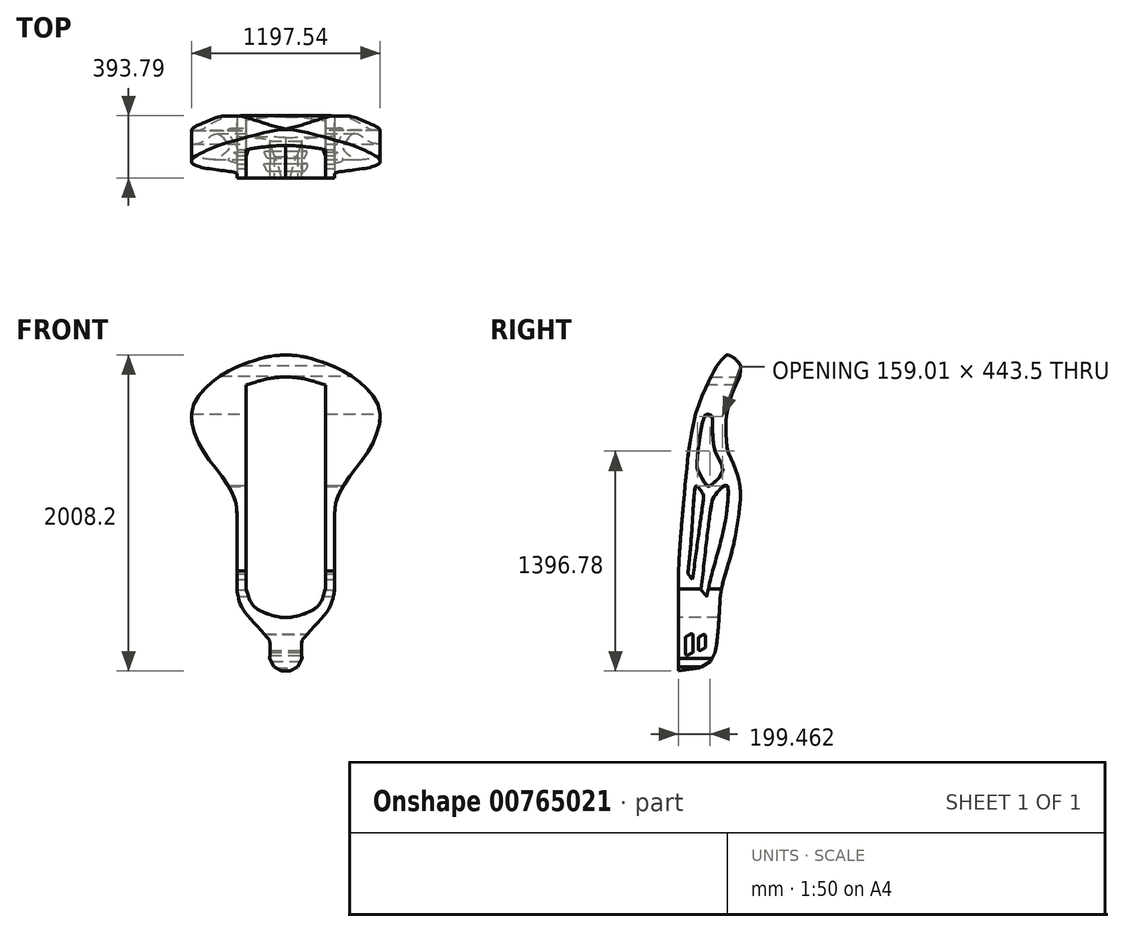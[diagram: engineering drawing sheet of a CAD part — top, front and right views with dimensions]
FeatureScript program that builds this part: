
annotation { "Feature Type Name" : "Feature", "Feature Type Description" : "" }
export const myFeature = defineFeature(function(context is Context, id is Id, definition is map)
    precondition{}
    {
        {
            var Q0;
            Q0=qCreatedBy(makeId("Front.planeOp"),FACE);
            var sketch = newSketch(context, id + "F0", { "sketchPlane" : qUnion([Q0])});
            skLineSegment(sketch, "E0", {"start": v(-255.28, -84.36) * mm, "end": v(252.72, -84.36) * mm});
            skLineSegment(sketch, "E1", {"start": v(0, -829.48) * mm, "end": v(0, 1173.27) * mm});
            skSolve(sketch);
        }
        {
            var Q0;
            Q0=qCreatedBy(makeId("Right.planeOp"),FACE);
            var sketch = newSketch(context, id + "F1", { "sketchPlane" : qUnion([Q0])});
            skLineSegment(sketch, "E2.0", {"start": v(0, -829.48) * mm, "end": v(0, 1173.27) * mm});
            skSolve(sketch);
        }
        {
            var Q0;
            Q0=qCreatedBy(makeId("Front.planeOp"),FACE);
            var sketch = newSketch(context, id + "F2", { "sketchPlane" : qUnion([Q0])});
            skFitSpline(sketch, "E3", {"points": [v(0, 1178.72) * mm, v(-131.61, 1163.15) * mm, v(-387.55, 1062.86) * mm, v(-534.54, 943.54) * mm, v(-586.42, 860.53) * mm, v(-598.52, 786.17) * mm, v(-593.33, 730.83) * mm, v(-536.94, 587.44) * mm, v(-445.29, 459.48) * mm, v(-334.61, 291.74) * mm, v(-310.9, 168.96) * mm], "startDerivative": vector(-1185.5, -55.3) * mm, "endDerivative": vector(0, -1218.83) * mm});
            skLineSegment(sketch, "E4", {"start": v(-310.9, 168.96) * mm, "end": v(-310.9, -308.33) * mm});
            skFitSpline(sketch, "E5", {"points": [v(-310.9, -308.33) * mm, v(-292.5, -393.37) * mm, v(-233.06, -486.5) * mm, v(-109.25, -625.95) * mm, v(-101.61, -641.2) * mm, v(-101.61, -747.96) * mm], "startDerivative": vector(68.26, -452.87) * mm, "endDerivative": vector(-14.07, -627.34) * mm});
            skLineSegment(sketch, "E6", {"start": v(-101.61, -747.96) * mm, "end": v(-75.98, -803.52) * mm});
            skLineSegment(sketch, "E7", {"start": v(-75.98, -803.52) * mm, "end": v(-19.8, -832.39) * mm});
            skLineSegment(sketch, "E8", {"start": v(-19.8, -832.39) * mm, "end": v(0, -832.39) * mm});
            skLineSegment(sketch, "E9", {"start": v(0, 1178.72) * mm, "end": v(0, -832.39) * mm, "construction": true});
            skLineSegment(sketch, "E10.MirrorCS", {"start": v(75.98, -803.52) * mm, "end": v(19.8, -832.39) * mm});
            skLineSegment(sketch, "E11.MirrorCS", {"start": v(101.61, -747.96) * mm, "end": v(75.98, -803.52) * mm});
            skLineSegment(sketch, "E12.MirrorCS", {"start": v(19.8, -832.39) * mm, "end": v(0, -832.39) * mm});
            skFitSpline(sketch, "E13.MirrorCS", {"points": [v(310.9, -308.33) * mm, v(292.5, -393.37) * mm, v(233.06, -486.5) * mm, v(109.25, -625.95) * mm, v(101.61, -641.2) * mm, v(101.61, -747.96) * mm], "startDerivative": vector(-68.26, -452.87) * mm, "endDerivative": vector(14.07, -627.34) * mm});
            skLineSegment(sketch, "E14.MirrorCS", {"start": v(310.9, 168.96) * mm, "end": v(310.9, -308.33) * mm});
            skFitSpline(sketch, "E15.MirrorCS", {"points": [v(0, 1178.72) * mm, v(131.61, 1163.15) * mm, v(387.55, 1062.86) * mm, v(534.54, 943.54) * mm, v(586.42, 860.53) * mm, v(598.52, 786.17) * mm, v(593.33, 730.83) * mm, v(536.94, 587.44) * mm, v(445.29, 459.48) * mm, v(334.61, 291.74) * mm, v(310.9, 168.96) * mm], "startDerivative": vector(1185.5, -55.3) * mm, "endDerivative": vector(0, -1218.83) * mm});
            skSolve(sketch);
        }
        {
            var Q0;
            Q0=qSketchRegion(id+"F2",true);
            extrude(context, id + "F3", {"entities" : qUnion([Q0]), "oppositeDirection" : true, "depth" : 523.24 * mm});
        }
        {
            var Q0;
            Q0=qCreatedBy(makeId("Right.planeOp"),FACE);
            var sketch = newSketch(context, id + "F4", { "sketchPlane" : qUnion([Q0])});
            skLineSegment(sketch, "E16.0", {"start": v(523.24, 1178.72) * mm, "end": v(0, 1178.72) * mm, "construction": true});
            skLineSegment(sketch, "E17.0", {"start": v(0, -829.48) * mm, "end": v(0, 1173.27) * mm, "construction": true});
            skFitSpline(sketch, "E18", {"points": [v(0, -829.48) * mm, v(0, -194.12) * mm, v(23.27, 143.63) * mm, v(62.09, 547.37) * mm, v(96.06, 753.12) * mm, v(140.7, 898.7) * mm, v(255.63, 1125.36) * mm, v(307.85, 1178.72) * mm], "startDerivative": vector(-39.4, 3171.5) * mm, "endDerivative": vector(647.49, 513.12) * mm});
            skFitSpline(sketch, "E19", {"points": [v(231.85, -711.1) * mm, v(246.25, -618.56) * mm, v(260.64, -421.14) * mm, v(272.98, -301.86) * mm, v(336.73, -75.65) * mm, v(375.8, 123.83) * mm, v(392.26, 269.84) * mm, v(390.2, 337.7) * mm, v(373.75, 417.9) * mm, v(338.79, 506.34) * mm, v(307.85, 586.06) * mm, v(301.76, 738.3) * mm, v(305.26, 807.25) * mm, v(341.33, 935.08) * mm, v(361.45, 984.12) * mm, v(390.27, 1044.51) * mm], "startDerivative": vector(248.18, 1330.22) * mm, "endDerivative": vector(610.21, 1265.5) * mm});
            skFitSpline(sketch, "E20", {"points": [v(307.85, 1178.72) * mm, v(350.06, 1159.99) * mm, v(393.79, 1113) * mm], "startDerivative": vector(77.42, 1.05) * mm, "endDerivative": vector(93.18, -122.51) * mm});
            skLineSegment(sketch, "E21", {"start": v(393.79, 1113) * mm, "end": v(390.27, 1044.51) * mm});
            skLineSegment(sketch, "E22", {"start": v(231.85, -711.1) * mm, "end": v(202.08, -767.87) * mm});
            skLineSegment(sketch, "E23", {"start": v(202.08, -767.87) * mm, "end": v(135.63, -809.16) * mm});
            skLineSegment(sketch, "E24", {"start": v(135.63, -809.16) * mm, "end": v(0, -829.48) * mm});
            skLineSegment(sketch, "E25.bottom", {"start": v(647.82, 1273) * mm, "end": v(-285.83, 1273) * mm});
            skLineSegment(sketch, "E25.top", {"start": v(647.82, -902.76) * mm, "end": v(-285.83, -902.76) * mm});
            skLineSegment(sketch, "E25.left", {"start": v(647.82, 1273) * mm, "end": v(647.82, -902.76) * mm});
            skLineSegment(sketch, "E25.right", {"start": v(-285.83, 1273) * mm, "end": v(-285.83, -902.76) * mm});
            skSolve(sketch);
        }
        {
            var Q0;
            Q0=qSketchRegion(id+"F4",true);
            extrude(context, id + "F5", {"entities" : qUnion([Q0]), "operationType" : NewBodyOperationType.REMOVE, "endBound" : BoundingType.THROUGH_ALL, "oppositeDirection" : true, "depth" : 25.4 * mm, "hasSecondDirection" : true, "secondDirectionBound" : SecondDirectionBoundingType.THROUGH_ALL, "secondDirectionOppositeDirection" : false, "secondDirectionDepth" : 25.4 * mm});
        }
        {
            var Q0;
            Q0=qCreatedBy(makeId("Front.planeOp"),FACE);
            var sketch = newSketch(context, id + "F6", { "sketchPlane" : qUnion([Q0])});
            skFitSpline(sketch, "E26.0.0", {"points": [v(310.9, 168.96) * mm, v(310.9, 172.92) * mm, v(311.01, 180.84) * mm, v(311.52, 192.71) * mm, v(312.42, 204.58) * mm, v(313.76, 216.32) * mm, v(315.53, 227.96) * mm, v(317.77, 239.47) * mm, v(320.48, 250.86) * mm, v(323.66, 262.14) * mm, v(327.32, 273.28) * mm, v(331.45, 284.3) * mm, v(334.9, 292.49) * mm, v(337.34, 297.9) * mm, v(339, 301.5) * mm, v(341.13, 305.97) * mm, v(343.77, 311.28) * mm, v(347.39, 318.29) * mm, v(353.96, 330.38) * mm, v(363.92, 347.25) * mm, v(376.6, 366.98) * mm, v(389.85, 386.32) * mm, v(403.55, 405.34) * mm, v(422.3, 430.35) * mm, v(441.63, 454.96) * mm, v(461.2, 479.4) * mm, v(475.83, 497.74) * mm, v(487.82, 513.17) * mm, v(497.17, 525.67) * mm, v(504.04, 535.15) * mm, v(509.62, 543.14) * mm, v(513.98, 549.6) * mm, v(517.2, 554.49) * mm, v(520.38, 559.4) * mm, v(524.51, 565.99) * mm, v(529.53, 574.29) * mm, v(535.3, 584.36) * mm, v(540.79, 594.54) * mm, v(546.04, 604.83) * mm, v(552.77, 618.66) * mm, v(560.68, 636.15) * mm, v(569.48, 657.43) * mm, v(576.26, 675.38) * mm, v(581.32, 689.88) * mm, v(584.93, 700.83) * mm, v(588.31, 711.88) * mm, v(591.41, 722.94) * mm, v(594.16, 734.03) * mm, v(596.4, 745.18) * mm, v(598, 756.4) * mm, v(598.64, 765.83) * mm, v(598.8, 773.4) * mm, v(598.75, 779.1) * mm, v(598.59, 784.81) * mm, v(598.34, 790.53) * mm, v(598.02, 796.22) * mm, v(597.48, 803.78) * mm, v(596.58, 813.15) * mm, v(595.1, 824.27) * mm, v(593.19, 835.25) * mm, v(590.76, 846.1) * mm, v(588.26, 855.02) * mm, v(585.92, 862.07) * mm, v(584.3, 866.44) * mm, v(582.93, 869.92) * mm, v(581.85, 872.52) * mm, v(580.74, 875.1) * mm, v(579.2, 878.5) * mm, v(577.19, 882.7) * mm, v(573.79, 889.32) * mm, v(569.22, 897.37) * mm, v(563.27, 906.73) * mm, v(556.93, 915.84) * mm, v(550.23, 924.73) * mm, v(544.4, 931.98) * mm, v(539.6, 937.7) * mm, v(535.95, 941.94) * mm, v(532.24, 946.15) * mm, v(527.24, 951.7) * mm, v(520.9, 958.53) * mm, v(510.5, 969.24) * mm, v(497.12, 982.22) * mm, v(483.2, 994.68) * mm, v(471.76, 1004.34) * mm, v(463.03, 1011.43) * mm, v(455.62, 1017.22) * mm, v(449.62, 1021.77) * mm, v(443.58, 1026.27) * mm, v(435.96, 1031.77) * mm, v(423.63, 1040.35) * mm, v(407.95, 1050.64) * mm, v(388.73, 1062.32) * mm, v(369.1, 1073.34) * mm, v(349.12, 1083.78) * mm, v(328.84, 1093.7) * mm, v(308.28, 1103.15) * mm, v(287.47, 1112.15) * mm, v(269.94, 1119.29) * mm, v(255.8, 1124.78) * mm, v(241.6, 1130.13) * mm, v(223.8, 1136.5) * mm, v(202.35, 1143.68) * mm, v(180.8, 1150.35) * mm, v(159.14, 1156.47) * mm, v(140.96, 1161.06) * mm, v(126.3, 1164.36) * mm, v(111.54, 1167.4) * mm, v(92.9, 1170.7) * mm, v(70.17, 1173.8) * mm, v(47.07, 1176.07) * mm, v(23.64, 1177.61) * mm, v(7.88, 1178.35) * mm, v(0, 1178.72) * mm]});
            skFitSpline(sketch, "E26.0.1", {"points": [v(0, 1178.72) * mm, v(-7.88, 1178.35) * mm, v(-23.64, 1177.61) * mm, v(-47.07, 1176.07) * mm, v(-70.17, 1173.8) * mm, v(-92.9, 1170.7) * mm, v(-111.54, 1167.4) * mm, v(-126.3, 1164.36) * mm, v(-140.96, 1161.06) * mm, v(-159.14, 1156.47) * mm, v(-180.8, 1150.35) * mm, v(-202.35, 1143.68) * mm, v(-223.8, 1136.5) * mm, v(-241.6, 1130.13) * mm, v(-255.8, 1124.78) * mm, v(-269.94, 1119.29) * mm, v(-287.47, 1112.15) * mm, v(-308.28, 1103.15) * mm, v(-328.84, 1093.7) * mm, v(-349.12, 1083.78) * mm, v(-369.1, 1073.34) * mm, v(-388.73, 1062.32) * mm, v(-407.95, 1050.64) * mm, v(-423.63, 1040.35) * mm, v(-435.96, 1031.77) * mm, v(-443.58, 1026.27) * mm, v(-449.62, 1021.77) * mm, v(-455.62, 1017.22) * mm, v(-463.03, 1011.43) * mm, v(-471.76, 1004.34) * mm, v(-483.2, 994.68) * mm, v(-497.12, 982.22) * mm, v(-510.5, 969.24) * mm, v(-520.9, 958.53) * mm, v(-527.24, 951.7) * mm, v(-532.24, 946.15) * mm, v(-535.95, 941.94) * mm, v(-539.6, 937.7) * mm, v(-544.4, 931.98) * mm, v(-550.23, 924.73) * mm, v(-556.93, 915.84) * mm, v(-563.27, 906.73) * mm, v(-569.22, 897.37) * mm, v(-573.79, 889.32) * mm, v(-577.19, 882.7) * mm, v(-579.2, 878.5) * mm, v(-580.74, 875.1) * mm, v(-581.85, 872.52) * mm, v(-582.93, 869.92) * mm, v(-584.3, 866.44) * mm, v(-585.92, 862.07) * mm, v(-588.26, 855.02) * mm, v(-590.76, 846.1) * mm, v(-593.19, 835.25) * mm, v(-595.1, 824.27) * mm, v(-596.58, 813.15) * mm, v(-597.48, 803.78) * mm, v(-598.02, 796.22) * mm, v(-598.34, 790.53) * mm, v(-598.59, 784.81) * mm, v(-598.75, 779.1) * mm, v(-598.8, 773.4) * mm, v(-598.64, 765.83) * mm, v(-598, 756.4) * mm, v(-596.4, 745.18) * mm, v(-594.16, 734.03) * mm, v(-591.41, 722.94) * mm, v(-588.31, 711.88) * mm, v(-584.93, 700.83) * mm, v(-581.32, 689.88) * mm, v(-576.26, 675.38) * mm, v(-569.48, 657.43) * mm, v(-560.68, 636.15) * mm, v(-552.77, 618.66) * mm, v(-546.04, 604.83) * mm, v(-540.79, 594.54) * mm, v(-535.3, 584.36) * mm, v(-529.53, 574.29) * mm, v(-524.51, 565.99) * mm, v(-520.38, 559.4) * mm, v(-517.2, 554.49) * mm, v(-513.98, 549.6) * mm, v(-509.62, 543.14) * mm, v(-504.04, 535.15) * mm, v(-497.17, 525.67) * mm, v(-487.82, 513.17) * mm, v(-475.83, 497.74) * mm, v(-461.2, 479.4) * mm, v(-441.63, 454.96) * mm, v(-422.3, 430.35) * mm, v(-403.55, 405.34) * mm, v(-389.85, 386.32) * mm, v(-376.6, 366.98) * mm, v(-363.92, 347.25) * mm, v(-353.96, 330.38) * mm, v(-347.39, 318.29) * mm, v(-343.77, 311.28) * mm, v(-341.13, 305.97) * mm, v(-339, 301.5) * mm, v(-337.34, 297.9) * mm, v(-334.9, 292.49) * mm, v(-331.45, 284.3) * mm, v(-327.32, 273.28) * mm, v(-323.66, 262.14) * mm, v(-320.48, 250.86) * mm, v(-317.77, 239.47) * mm, v(-315.53, 227.96) * mm, v(-313.76, 216.32) * mm, v(-312.42, 204.58) * mm, v(-311.52, 192.71) * mm, v(-311.01, 180.84) * mm, v(-310.9, 172.92) * mm, v(-310.9, 168.96) * mm]});
            skFitSpline(sketch, "E26.0.2", {"points": [v(-310.9, 1178.72) * mm, v(-310.9, 1165.88) * mm, v(-310.9, 1129.35) * mm, v(-310.9, 894.02) * mm, v(-310.9, 753.1) * mm, v(-310.9, 541.34) * mm, v(-310.9, 129.24) * mm, v(-310.9, -197.5) * mm, v(-310.9, -597.98) * mm, v(-310.9, -829.48) * mm]});
            skFitSpline(sketch, "E26.0.4", {"points": [v(310.9, 1178.72) * mm, v(310.9, 1165.88) * mm, v(310.9, 1129.35) * mm, v(310.9, 894.02) * mm, v(310.9, 753.1) * mm, v(310.9, 541.34) * mm, v(310.9, 129.24) * mm, v(310.9, -197.5) * mm, v(310.9, -597.98) * mm, v(310.9, -829.48) * mm]});
            skLineSegment(sketch, "E26.1.0", {"start": v(-25.46, -829.48) * mm, "end": v(25.46, -829.48) * mm});
            skLineSegment(sketch, "E26.1.1", {"start": v(25.46, -829.48) * mm, "end": v(75.98, -803.52) * mm});
            skLineSegment(sketch, "E26.1.2", {"start": v(75.98, -803.52) * mm, "end": v(101.61, -747.96) * mm});
            skFitSpline(sketch, "E26.1.3", {"points": [v(101.61, -747.96) * mm, v(100.6, -702.9) * mm, v(99.19, -639.84) * mm, v(107.99, -625.42) * mm, v(242.04, -482.32) * mm, v(297.07, -400.14) * mm, v(306.48, -337.69) * mm, v(310.9, -308.33) * mm]});
            skLineSegment(sketch, "E26.1.4", {"start": v(310.9, -308.33) * mm, "end": v(310.9, -194.12) * mm});
            skLineSegment(sketch, "E26.1.6", {"start": v(-310.9, -194.12) * mm, "end": v(-310.9, -308.33) * mm});
            skFitSpline(sketch, "E26.1.7", {"points": [v(-310.9, -308.33) * mm, v(-306.48, -337.69) * mm, v(-297.07, -400.14) * mm, v(-242.04, -482.32) * mm, v(-107.99, -625.42) * mm, v(-99.19, -639.84) * mm, v(-100.6, -702.9) * mm, v(-101.61, -747.96) * mm]});
            skLineSegment(sketch, "E26.1.8", {"start": v(-101.61, -747.96) * mm, "end": v(-75.98, -803.52) * mm});
            skLineSegment(sketch, "E26.1.9", {"start": v(-75.98, -803.52) * mm, "end": v(-25.46, -829.48) * mm});
            skFitSpline(sketch, "E27.0", {"points": [v(252.49, 1178.72) * mm, v(252.49, 1176.05) * mm, v(252.49, 1170.7) * mm, v(252.49, 1161.88) * mm, v(252.49, 1153.2) * mm, v(252.49, 1145.03) * mm, v(252.49, 1138.21) * mm, v(252.49, 1131.86) * mm, v(252.49, 1126.33) * mm, v(252.49, 1120.47) * mm, v(252.49, 1112.57) * mm, v(252.49, 1102.24) * mm, v(252.49, 1091.15) * mm, v(252.49, 1075.45) * mm, v(252.49, 1054.35) * mm, v(252.49, 1027.31) * mm, v(252.49, 999.24) * mm, v(252.49, 970.82) * mm, v(252.49, 947.39) * mm, v(252.49, 929.14) * mm, v(252.49, 915.78) * mm, v(252.49, 905) * mm, v(252.49, 896.62) * mm, v(252.49, 888.42) * mm, v(252.49, 878.47) * mm, v(252.49, 866.97) * mm, v(252.49, 855.86) * mm, v(252.49, 841.48) * mm, v(252.49, 824.18) * mm, v(252.49, 804.08) * mm, v(252.49, 787.52) * mm, v(252.49, 774.16) * mm, v(252.49, 764.04) * mm, v(252.49, 753.75) * mm, v(252.49, 743.24) * mm, v(252.49, 732.5) * mm, v(252.49, 717.85) * mm, v(252.49, 698.88) * mm, v(252.49, 674.93) * mm, v(252.49, 649.7) * mm, v(252.49, 623.06) * mm, v(252.49, 599.58) * mm, v(252.49, 579.97) * mm, v(252.49, 564.84) * mm, v(252.49, 549.27) * mm, v(252.49, 533.23) * mm, v(252.49, 516.77) * mm, v(252.49, 494.3) * mm, v(252.49, 465.33) * mm, v(252.49, 429.42) * mm, v(252.49, 392.65) * mm, v(252.49, 355.3) * mm, v(252.49, 317.67) * mm, v(252.49, 280.02) * mm, v(252.49, 242.64) * mm, v(252.49, 211.96) * mm, v(252.49, 187.83) * mm, v(252.49, 169.99) * mm, v(252.49, 152.41) * mm, v(252.49, 135.17) * mm, v(252.49, 118.24) * mm, v(252.49, 96.04) * mm, v(252.49, 68.88) * mm, v(252.49, 36.94) * mm, v(252.49, -5.2) * mm, v(252.49, -57.8) * mm, v(252.49, -123.23) * mm, v(252.49, -193.46) * mm, v(252.49, -270.92) * mm, v(252.49, -354.56) * mm, v(252.49, -443.36) * mm, v(252.49, -536.28) * mm, v(252.49, -632.3) * mm, v(252.49, -730.37) * mm, v(252.49, -796.44) * mm, v(252.49, -829.48) * mm]});
            skLineSegment(sketch, "E27.1", {"start": v(252.49, -303.95) * mm, "end": v(252.49, -194.12) * mm});
            skFitSpline(sketch, "E27.2", {"points": [v(-253.14, -299.62) * mm, v(-252.43, -304.34) * mm, v(-251.04, -313.59) * mm, v(-248.9, -326.83) * mm, v(-246.64, -339.34) * mm, v(-244.16, -351.04) * mm, v(-241.87, -360.01) * mm, v(-239.89, -366.7) * mm, v(-238.33, -371.44) * mm, v(-236.7, -375.92) * mm, v(-234.93, -380.29) * mm, v(-233, -384.62) * mm, v(-230.88, -388.98) * mm, v(-228.53, -393.45) * mm, v(-225.03, -399.6) * mm, v(-219.88, -407.83) * mm, v(-213.46, -417.01) * mm, v(-207.47, -425.05) * mm, v(-202.53, -431.45) * mm, v(-197.12, -438.24) * mm, v(-192.22, -444.24) * mm, v(-188.05, -449.27) * mm, v(-183.72, -454.44) * mm, v(-178.01, -461.17) * mm, v(-170.8, -469.55) * mm, v(-160.77, -481.06) * mm, v(-147.7, -495.86) * mm, v(-131.75, -513.7) * mm, v(-118.69, -528.15) * mm, v(-108.67, -539.2) * mm, v(-101.43, -547.18) * mm, v(-94.55, -554.77) * mm, v(-88.07, -561.91) * mm, v(-82.07, -568.55) * mm, v(-77.52, -573.61) * mm, v(-74.16, -577.37) * mm, v(-71.79, -580.04) * mm, v(-69.57, -582.55) * mm, v(-67.84, -584.52) * mm, v(-66.52, -586.03) * mm, v(-65.73, -586.95) * mm, v(-65.11, -587.67) * mm, v(-64.5, -588.38) * mm, v(-63.73, -589.3) * mm, v(-62.77, -590.45) * mm, v(-61.41, -592.1) * mm, v(-59.56, -594.43) * mm, v(-57.04, -597.86) * mm, v(-54.26, -602.1) * mm, v(-51.42, -607.18) * mm, v(-48.83, -612.85) * mm, v(-47.11, -617.68) * mm, v(-46.04, -621.36) * mm, v(-45.38, -623.98) * mm, v(-44.84, -626.43) * mm, v(-44.42, -628.7) * mm, v(-44.08, -630.78) * mm, v(-43.85, -632.37) * mm, v(-43.7, -633.57) * mm, v(-43.59, -634.43) * mm, v(-43.49, -635.27) * mm, v(-43.37, -636.39) * mm, v(-43.23, -637.76) * mm, v(-43.04, -639.93) * mm, v(-42.83, -642.61) * mm, v(-42.64, -645.86) * mm, v(-42.47, -649.16) * mm, v(-42.3, -653.68) * mm, v(-42.15, -659.57) * mm, v(-42.05, -667.07) * mm, v(-42.02, -675) * mm, v(-42.04, -683.35) * mm, v(-42.12, -692.08) * mm, v(-42.24, -701.12) * mm, v(-42.44, -713.55) * mm, v(-42.77, -729.62) * mm, v(-43.06, -742.74) * mm, v(-43.2, -749.27) * mm]});
            skLineSegment(sketch, "E27.3", {"start": v(-252.49, -194.12) * mm, "end": v(-252.49, -303.95) * mm});
            skFitSpline(sketch, "E27.4", {"points": [v(-252.49, 1178.72) * mm, v(-252.49, 1176.05) * mm, v(-252.49, 1170.7) * mm, v(-252.49, 1161.88) * mm, v(-252.49, 1153.2) * mm, v(-252.49, 1145.03) * mm, v(-252.49, 1138.21) * mm, v(-252.49, 1131.86) * mm, v(-252.49, 1126.33) * mm, v(-252.49, 1120.47) * mm, v(-252.49, 1112.57) * mm, v(-252.49, 1102.24) * mm, v(-252.49, 1091.15) * mm, v(-252.49, 1075.45) * mm, v(-252.49, 1054.35) * mm, v(-252.49, 1027.31) * mm, v(-252.49, 999.24) * mm, v(-252.49, 970.82) * mm, v(-252.49, 947.39) * mm, v(-252.49, 929.14) * mm, v(-252.49, 915.78) * mm, v(-252.49, 905) * mm, v(-252.49, 896.62) * mm, v(-252.49, 888.42) * mm, v(-252.49, 878.47) * mm, v(-252.49, 866.97) * mm, v(-252.49, 855.86) * mm, v(-252.49, 841.48) * mm, v(-252.49, 824.18) * mm, v(-252.49, 804.08) * mm, v(-252.49, 787.52) * mm, v(-252.49, 774.16) * mm, v(-252.49, 764.04) * mm, v(-252.49, 753.75) * mm, v(-252.49, 743.24) * mm, v(-252.49, 732.5) * mm, v(-252.49, 717.85) * mm, v(-252.49, 698.88) * mm, v(-252.49, 674.93) * mm, v(-252.49, 649.7) * mm, v(-252.49, 623.06) * mm, v(-252.49, 599.58) * mm, v(-252.49, 579.97) * mm, v(-252.49, 564.84) * mm, v(-252.49, 549.27) * mm, v(-252.49, 533.23) * mm, v(-252.49, 516.77) * mm, v(-252.49, 494.3) * mm, v(-252.49, 465.33) * mm, v(-252.49, 429.42) * mm, v(-252.49, 392.65) * mm, v(-252.49, 355.3) * mm, v(-252.49, 317.67) * mm, v(-252.49, 280.02) * mm, v(-252.49, 242.64) * mm, v(-252.49, 211.96) * mm, v(-252.49, 187.83) * mm, v(-252.49, 169.99) * mm, v(-252.49, 152.41) * mm, v(-252.49, 135.17) * mm, v(-252.49, 118.24) * mm, v(-252.49, 96.04) * mm, v(-252.49, 68.88) * mm, v(-252.49, 36.94) * mm, v(-252.49, -5.2) * mm, v(-252.49, -57.8) * mm, v(-252.49, -123.23) * mm, v(-252.49, -193.46) * mm, v(-252.49, -270.92) * mm, v(-252.49, -354.56) * mm, v(-252.49, -443.36) * mm, v(-252.49, -536.28) * mm, v(-252.49, -632.3) * mm, v(-252.49, -730.37) * mm, v(-252.49, -796.44) * mm, v(-252.49, -829.48) * mm]});
            skFitSpline(sketch, "E27.5", {"points": [v(2.72, 1120.36) * mm, v(-1.21, 1120.18) * mm, v(-7.05, 1119.9) * mm, v(-14.68, 1119.52) * mm, v(-20.33, 1119.22) * mm, v(-25.9, 1118.89) * mm, v(-31.42, 1118.53) * mm, v(-36.87, 1118.15) * mm, v(-42.26, 1117.73) * mm, v(-47.59, 1117.27) * mm, v(-52.88, 1116.77) * mm, v(-58.13, 1116.23) * mm, v(-63.33, 1115.65) * mm, v(-68.49, 1115.02) * mm, v(-73.62, 1114.34) * mm, v(-78.73, 1113.62) * mm, v(-83.81, 1112.85) * mm, v(-88.87, 1112.03) * mm, v(-95.6, 1110.88) * mm, v(-102.29, 1109.63) * mm, v(-108.96, 1108.29) * mm, v(-113.95, 1107.23) * mm, v(-118.94, 1106.13) * mm, v(-125.6, 1104.6) * mm, v(-132.29, 1102.97) * mm, v(-138.98, 1101.26) * mm, v(-144.02, 1099.93) * mm, v(-149.06, 1098.57) * mm, v(-155.79, 1096.7) * mm, v(-167.57, 1093.29) * mm, v(-184.44, 1088.07) * mm, v(-201.3, 1082.43) * mm, v(-214.77, 1077.69) * mm, v(-224.86, 1074) * mm, v(-234.94, 1070.21) * mm, v(-244.96, 1066.32) * mm, v(-254.93, 1062.32) * mm, v(-268.14, 1056.86) * mm, v(-284.5, 1049.79) * mm, v(-303.81, 1040.91) * mm, v(-319.6, 1033.18) * mm, v(-332.03, 1026.8) * mm, v(-341.23, 1021.9) * mm, v(-348.78, 1017.73) * mm, v(-354.76, 1014.34) * mm, v(-359.2, 1011.77) * mm, v(-363.6, 1009.17) * mm, v(-369.46, 1005.65) * mm, v(-376.7, 1001.16) * mm, v(-385.3, 995.63) * mm, v(-393.78, 989.95) * mm, v(-402.17, 984.12) * mm, v(-409.06, 979.13) * mm, v(-414.52, 975.07) * mm, v(-419.95, 970.95) * mm, v(-426.63, 965.73) * mm, v(-434.5, 959.34) * mm, v(-444.8, 950.64) * mm, v(-457.3, 939.46) * mm, v(-469.27, 927.85) * mm, v(-477.37, 919.5) * mm, v(-481.91, 914.66) * mm, v(-485.28, 911) * mm, v(-488.6, 907.3) * mm, v(-491.89, 903.58) * mm, v(-495.09, 899.85) * mm, v(-498.2, 896.15) * mm, v(-501.2, 892.47) * mm, v(-505.08, 887.57) * mm, v(-509.64, 881.51) * mm, v(-514.65, 874.32) * mm, v(-519.15, 867.22) * mm, v(-522.46, 861.37) * mm, v(-524.86, 856.71) * mm, v(-526.25, 853.8) * mm, v(-527.3, 851.48) * mm, v(-528.06, 849.73) * mm, v(-528.78, 847.98) * mm, v(-529.47, 846.24) * mm, v(-530.13, 844.5) * mm, v(-530.75, 842.77) * mm, v(-531.34, 841.03) * mm, v(-532.1, 838.66) * mm, v(-532.83, 836.23) * mm, v(-533.52, 833.72) * mm, v(-534.18, 831.17) * mm, v(-534.96, 827.9) * mm, v(-536.1, 822.48) * mm, v(-537.34, 815.44) * mm, v(-538.33, 808.04) * mm, v(-538.97, 801.94) * mm, v(-539.3, 798.05) * mm, v(-539.55, 794.89) * mm, v(-539.7, 792.5) * mm, v(-539.85, 790.09) * mm, v(-539.96, 788.05) * mm, v(-540.04, 786.42) * mm, v(-540.1, 785.19) * mm, v(-540.14, 783.96) * mm, v(-540.19, 782.73) * mm, v(-540.23, 781.52) * mm, v(-540.28, 779.94) * mm, v(-540.32, 778.03) * mm, v(-540.35, 775.84) * mm, v(-540.35, 773.74) * mm, v(-540.33, 772.07) * mm, v(-540.3, 770.77) * mm, v(-540.27, 769.82) * mm, v(-540.23, 768.9) * mm, v(-540.17, 767.65) * mm, v(-540.08, 766.12) * mm, v(-539.96, 764.6) * mm, v(-539.85, 763.4) * mm, v(-539.76, 762.51) * mm, v(-539.66, 761.62) * mm, v(-539.52, 760.4) * mm, v(-539.32, 758.88) * mm, v(-539.04, 757) * mm, v(-538.73, 755.07) * mm, v(-538.37, 753.1) * mm, v(-537.85, 750.4) * mm, v(-537.25, 747.59) * mm, v(-536.58, 744.67) * mm, v(-536.04, 742.44) * mm, v(-535.47, 740.17) * mm, v(-534.87, 737.85) * mm, v(-534.24, 735.5) * mm, v(-533.59, 733.13) * mm, v(-532.91, 730.74) * mm, v(-531.98, 727.52) * mm, v(-530.76, 723.46) * mm, v(-528.71, 716.9) * mm, v(-526, 708.66) * mm, v(-523.11, 700.39) * mm, v(-520.71, 693.78) * mm, v(-518.87, 688.83) * mm, v(-516.98, 683.89) * mm, v(-515.05, 678.96) * mm, v(-513.09, 674.04) * mm, v(-511.08, 669.14) * mm, v(-509.04, 664.27) * mm, v(-506.96, 659.4) * mm, v(-504.85, 654.58) * mm, v(-502.7, 649.77) * mm, v(-500.5, 645) * mm, v(-497.54, 638.68) * mm, v(-494.5, 632.43) * mm, v(-491.4, 626.28) * mm, v(-489.03, 621.71) * mm, v(-487.03, 617.96) * mm, v(-485.41, 614.97) * mm, v(-484.19, 612.75) * mm, v(-482.95, 610.54) * mm, v(-481.27, 607.6) * mm, v(-479.14, 603.92) * mm, v(-476.52, 599.52) * mm, v(-473.84, 595.15) * mm, v(-471.1, 590.78) * mm, v(-468.28, 586.41) * mm, v(-465.4, 582.06) * mm, v(-461.49, 576.26) * mm, v(-454.42, 566.13) * mm, v(-445.86, 554.52) * mm, v(-436.86, 542.8) * mm, v(-429.92, 533.92) * mm, v(-422.81, 524.96) * mm, v(-416.78, 517.4) * mm, v(-411.9, 511.3) * mm, v(-408.23, 506.71) * mm, v(-404.54, 502.09) * mm, v(-400.83, 497.44) * mm, v(-397.12, 492.76) * mm, v(-392.16, 486.5) * mm, v(-385.98, 478.63) * mm, v(-378.56, 469.1) * mm, v(-371.18, 459.47) * mm, v(-363.83, 449.75) * mm, v(-354.1, 436.64) * mm, v(-344.48, 423.3) * mm, v(-335.01, 409.65) * mm, v(-329.17, 400.98) * mm, v(-324.55, 393.95) * mm, v(-321.1, 388.63) * mm, v(-317.69, 383.25) * mm, v(-314.3, 377.82) * mm, v(-310.95, 372.33) * mm, v(-307.63, 366.76) * mm, v(-304.35, 361.12) * mm, v(-301.11, 355.4) * mm, v(-297.92, 349.6) * mm, v(-294.77, 343.7) * mm, v(-291.67, 337.7) * mm, v(-288.62, 331.58) * mm, v(-286.13, 326.37) * mm, v(-284.18, 322.14) * mm, v(-282.74, 318.93) * mm, v(-281.32, 315.7) * mm, v(-279.93, 312.45) * mm, v(-278.57, 309.18) * mm, v(-276.8, 304.8) * mm, v(-274.67, 299.29) * mm, v(-272.26, 292.63) * mm, v(-269.98, 285.93) * mm, v(-267.13, 276.92) * mm, v(-263.92, 265.57) * mm, v(-260.65, 251.8) * mm, v(-257.96, 237.93) * mm, v(-256.18, 226.33) * mm, v(-255.04, 217.04) * mm, v(-254.07, 207.74) * mm, v(-253.19, 196.15) * mm, v(-252.6, 182.43) * mm, v(-252.49, 173.42) * mm, v(-252.49, 168.96) * mm]});
            skLineSegment(sketch, "E27.6", {"start": v(-42.9, -735.75) * mm, "end": v(-31.37, -760.76) * mm});
            skLineSegment(sketch, "E27.7", {"start": v(-31.37, -760.76) * mm, "end": v(-11.33, -771.06) * mm});
            skFitSpline(sketch, "E27.8", {"points": [v(252.49, 168.96) * mm, v(252.49, 173.42) * mm, v(252.6, 182.43) * mm, v(253.19, 196.15) * mm, v(254.07, 207.74) * mm, v(255.04, 217.04) * mm, v(256.18, 226.33) * mm, v(257.96, 237.93) * mm, v(260.65, 251.8) * mm, v(263.92, 265.57) * mm, v(267.13, 276.92) * mm, v(269.98, 285.93) * mm, v(272.26, 292.63) * mm, v(274.67, 299.29) * mm, v(276.8, 304.8) * mm, v(278.57, 309.18) * mm, v(279.93, 312.45) * mm, v(281.32, 315.7) * mm, v(282.74, 318.93) * mm, v(284.18, 322.14) * mm, v(286.13, 326.37) * mm, v(288.62, 331.58) * mm, v(291.67, 337.7) * mm, v(294.77, 343.7) * mm, v(297.92, 349.6) * mm, v(301.11, 355.4) * mm, v(304.35, 361.12) * mm, v(307.63, 366.76) * mm, v(310.95, 372.33) * mm, v(314.3, 377.82) * mm, v(317.69, 383.25) * mm, v(321.1, 388.63) * mm, v(324.55, 393.95) * mm, v(329.17, 400.98) * mm, v(335.01, 409.65) * mm, v(344.48, 423.3) * mm, v(354.1, 436.64) * mm, v(363.83, 449.75) * mm, v(371.18, 459.47) * mm, v(378.56, 469.1) * mm, v(385.98, 478.63) * mm, v(392.16, 486.5) * mm, v(397.12, 492.76) * mm, v(400.83, 497.44) * mm, v(404.54, 502.09) * mm, v(408.23, 506.71) * mm, v(411.9, 511.3) * mm, v(416.78, 517.4) * mm, v(422.81, 524.96) * mm, v(429.92, 533.92) * mm, v(436.86, 542.8) * mm, v(445.86, 554.52) * mm, v(454.42, 566.13) * mm, v(461.49, 576.26) * mm, v(465.4, 582.06) * mm, v(468.28, 586.41) * mm, v(471.1, 590.78) * mm, v(473.84, 595.15) * mm, v(476.52, 599.52) * mm, v(479.14, 603.92) * mm, v(481.27, 607.6) * mm, v(482.95, 610.54) * mm, v(484.19, 612.75) * mm, v(485.41, 614.97) * mm, v(487.03, 617.96) * mm, v(489.03, 621.71) * mm, v(491.4, 626.28) * mm, v(494.5, 632.43) * mm, v(497.54, 638.68) * mm, v(500.5, 645) * mm, v(502.7, 649.77) * mm, v(504.85, 654.58) * mm, v(506.96, 659.4) * mm, v(509.04, 664.27) * mm, v(511.08, 669.14) * mm, v(513.09, 674.04) * mm, v(515.05, 678.96) * mm, v(516.98, 683.89) * mm, v(518.87, 688.83) * mm, v(520.71, 693.78) * mm, v(523.11, 700.39) * mm, v(526, 708.66) * mm, v(528.71, 716.9) * mm, v(530.76, 723.46) * mm, v(531.98, 727.52) * mm, v(532.91, 730.74) * mm, v(533.59, 733.13) * mm, v(534.24, 735.5) * mm, v(534.87, 737.85) * mm, v(535.47, 740.17) * mm, v(536.04, 742.44) * mm, v(536.58, 744.67) * mm, v(537.25, 747.59) * mm, v(537.85, 750.4) * mm, v(538.37, 753.1) * mm, v(538.73, 755.07) * mm, v(539.04, 757) * mm, v(539.32, 758.88) * mm, v(539.52, 760.4) * mm, v(539.66, 761.62) * mm, v(539.76, 762.51) * mm, v(539.85, 763.4) * mm, v(539.96, 764.6) * mm, v(540.08, 766.12) * mm, v(540.17, 767.65) * mm, v(540.23, 768.9) * mm, v(540.27, 769.82) * mm, v(540.3, 770.77) * mm, v(540.33, 772.07) * mm, v(540.35, 773.74) * mm, v(540.35, 775.84) * mm, v(540.32, 778.03) * mm, v(540.28, 779.94) * mm, v(540.23, 781.52) * mm, v(540.19, 782.73) * mm, v(540.14, 783.96) * mm, v(540.1, 785.19) * mm, v(540.04, 786.42) * mm, v(539.96, 788.05) * mm, v(539.85, 790.09) * mm, v(539.7, 792.5) * mm, v(539.55, 794.89) * mm, v(539.3, 798.05) * mm, v(538.97, 801.94) * mm, v(538.33, 808.04) * mm, v(537.34, 815.44) * mm, v(536.1, 822.48) * mm, v(534.96, 827.9) * mm, v(534.18, 831.17) * mm, v(533.52, 833.72) * mm, v(532.83, 836.23) * mm, v(532.1, 838.66) * mm, v(531.34, 841.03) * mm, v(530.75, 842.77) * mm, v(530.13, 844.5) * mm, v(529.47, 846.24) * mm, v(528.78, 847.98) * mm, v(528.06, 849.73) * mm, v(527.3, 851.48) * mm, v(526.25, 853.8) * mm, v(524.86, 856.71) * mm, v(522.46, 861.37) * mm, v(519.15, 867.22) * mm, v(514.65, 874.32) * mm, v(509.64, 881.51) * mm, v(505.08, 887.57) * mm, v(501.2, 892.47) * mm, v(498.2, 896.15) * mm, v(495.09, 899.85) * mm, v(491.89, 903.58) * mm, v(488.6, 907.3) * mm, v(485.28, 911) * mm, v(481.91, 914.66) * mm, v(477.37, 919.5) * mm, v(469.27, 927.85) * mm, v(457.3, 939.46) * mm, v(444.8, 950.64) * mm, v(434.5, 959.34) * mm, v(426.63, 965.73) * mm, v(419.95, 970.95) * mm, v(414.52, 975.07) * mm, v(409.06, 979.13) * mm, v(402.17, 984.12) * mm, v(393.78, 989.95) * mm, v(385.3, 995.63) * mm, v(376.7, 1001.16) * mm, v(369.46, 1005.65) * mm, v(363.6, 1009.17) * mm, v(359.2, 1011.77) * mm, v(354.76, 1014.34) * mm, v(348.78, 1017.73) * mm, v(341.23, 1021.9) * mm, v(332.03, 1026.8) * mm, v(319.6, 1033.18) * mm, v(303.81, 1040.91) * mm, v(284.5, 1049.79) * mm, v(268.14, 1056.86) * mm, v(254.93, 1062.32) * mm, v(244.96, 1066.32) * mm, v(234.94, 1070.21) * mm, v(224.86, 1074) * mm, v(214.77, 1077.69) * mm, v(201.3, 1082.43) * mm, v(184.44, 1088.07) * mm, v(167.57, 1093.29) * mm, v(155.79, 1096.7) * mm, v(149.06, 1098.57) * mm, v(144.02, 1099.93) * mm, v(138.98, 1101.26) * mm, v(132.29, 1102.97) * mm, v(125.6, 1104.6) * mm, v(118.94, 1106.13) * mm, v(113.95, 1107.23) * mm, v(108.96, 1108.29) * mm, v(102.29, 1109.63) * mm, v(95.6, 1110.88) * mm, v(88.87, 1112.03) * mm, v(83.81, 1112.85) * mm, v(78.73, 1113.62) * mm, v(73.62, 1114.34) * mm, v(68.49, 1115.02) * mm, v(63.33, 1115.65) * mm, v(58.13, 1116.23) * mm, v(52.88, 1116.77) * mm, v(47.59, 1117.27) * mm, v(42.26, 1117.73) * mm, v(36.87, 1118.15) * mm, v(31.42, 1118.53) * mm, v(25.9, 1118.89) * mm, v(20.33, 1119.22) * mm, v(14.68, 1119.52) * mm, v(7.05, 1119.9) * mm, v(1.21, 1120.18) * mm, v(-2.72, 1120.36) * mm]});
            skLineSegment(sketch, "E27.9", {"start": v(-11.33, -771.06) * mm, "end": v(11.33, -771.06) * mm});
            skLineSegment(sketch, "E27.10", {"start": v(11.33, -771.06) * mm, "end": v(31.37, -760.76) * mm});
            skLineSegment(sketch, "E27.11", {"start": v(31.37, -760.76) * mm, "end": v(42.9, -735.75) * mm});
            skFitSpline(sketch, "E27.12", {"points": [v(43.2, -749.27) * mm, v(43.06, -742.74) * mm, v(42.77, -729.62) * mm, v(42.44, -713.55) * mm, v(42.24, -701.12) * mm, v(42.12, -692.08) * mm, v(42.04, -683.35) * mm, v(42.02, -675) * mm, v(42.05, -667.07) * mm, v(42.15, -659.57) * mm, v(42.3, -653.68) * mm, v(42.47, -649.16) * mm, v(42.64, -645.86) * mm, v(42.83, -642.61) * mm, v(43.04, -639.93) * mm, v(43.23, -637.76) * mm, v(43.37, -636.39) * mm, v(43.49, -635.27) * mm, v(43.59, -634.43) * mm, v(43.7, -633.57) * mm, v(43.85, -632.37) * mm, v(44.08, -630.78) * mm, v(44.42, -628.7) * mm, v(44.84, -626.43) * mm, v(45.38, -623.98) * mm, v(46.04, -621.36) * mm, v(47.11, -617.68) * mm, v(48.83, -612.85) * mm, v(51.42, -607.18) * mm, v(54.26, -602.1) * mm, v(57.04, -597.86) * mm, v(59.56, -594.43) * mm, v(61.41, -592.1) * mm, v(62.77, -590.45) * mm, v(63.73, -589.3) * mm, v(64.5, -588.38) * mm, v(65.11, -587.67) * mm, v(65.73, -586.95) * mm, v(66.52, -586.03) * mm, v(67.84, -584.52) * mm, v(69.57, -582.55) * mm, v(71.79, -580.04) * mm, v(74.16, -577.37) * mm, v(77.52, -573.61) * mm, v(82.07, -568.55) * mm, v(88.07, -561.91) * mm, v(94.55, -554.77) * mm, v(101.43, -547.18) * mm, v(108.67, -539.2) * mm, v(118.69, -528.15) * mm, v(131.75, -513.7) * mm, v(147.7, -495.86) * mm, v(160.77, -481.06) * mm, v(170.8, -469.55) * mm, v(178.01, -461.17) * mm, v(183.72, -454.44) * mm, v(188.05, -449.27) * mm, v(192.22, -444.24) * mm, v(197.12, -438.24) * mm, v(202.53, -431.45) * mm, v(207.47, -425.05) * mm, v(213.46, -417.01) * mm, v(219.88, -407.83) * mm, v(225.03, -399.6) * mm, v(228.53, -393.45) * mm, v(230.88, -388.98) * mm, v(233, -384.62) * mm, v(234.93, -380.29) * mm, v(236.7, -375.92) * mm, v(238.33, -371.44) * mm, v(239.89, -366.7) * mm, v(241.87, -360.01) * mm, v(244.16, -351.04) * mm, v(246.64, -339.34) * mm, v(248.9, -326.83) * mm, v(251.04, -313.59) * mm, v(252.43, -304.34) * mm, v(253.14, -299.62) * mm]});
            skFitSpline(sketch, "E28", {"points": [v(-533.6, 733.18) * mm, v(-538.35, 807.6) * mm, v(-445.42, 899.69) * mm, v(-126.67, 1025.13) * mm, v(0, 1037.47) * mm], "startDerivative": vector(-100.12, 437.17) * mm, "endDerivative": vector(474.07, -1.36) * mm});
            skFitSpline(sketch, "E29", {"points": [v(-252.49, -303.95) * mm, v(-214.34, -403.54) * mm, v(-149.63, -452.26) * mm, v(-45.66, -485.7) * mm, v(0, -489.34) * mm], "startDerivative": vector(108.5, -392.67) * mm, "endDerivative": vector(217.04, -1.44) * mm});
            skLineSegment(sketch, "E30.0", {"start": v(0, -829.48) * mm, "end": v(0, 1173.27) * mm, "construction": true});
            skFitSpline(sketch, "E31.MirrorCS", {"points": [v(252.49, -303.95) * mm, v(214.34, -403.54) * mm, v(149.63, -452.26) * mm, v(45.66, -485.7) * mm, v(0, -489.34) * mm], "startDerivative": vector(-108.5, -392.67) * mm, "endDerivative": vector(-217.04, -1.44) * mm});
            skFitSpline(sketch, "E32.MirrorCS", {"points": [v(533.6, 733.18) * mm, v(538.35, 807.6) * mm, v(445.42, 899.69) * mm, v(126.67, 1025.13) * mm, v(0, 1037.47) * mm], "startDerivative": vector(100.12, 437.17) * mm, "endDerivative": vector(-474.07, -1.36) * mm});
            skSolve(sketch);
        }
        {
            var Q0;
            {var subQ14=sQuery(id+"F6.wireOp",EDGE,"E27.0");Q0=makeQuery(id+"F6.imprint","IMPRINT",FACE,{"disambiguationData":[TD([[makeQuery(id+"F6.imprint","IMPRINT",EDGE,{"derivedFrom":subQ14}),-1.0]])]});}
            extrude(context, id + "F7", {"entities" : qUnion([Q0]), "operationType" : NewBodyOperationType.REMOVE, "oppositeDirection" : true, "depth" : 617.22 * mm});
        }
        {
            var Q0;
            Q0=qCreatedBy(makeId("Right.planeOp"),FACE);
            var sketch = newSketch(context, id + "F8", { "sketchPlane" : qUnion([Q0])});
            skFitSpline(sketch, "E33", {"points": [v(278.97, 437.84) * mm, v(239.7, 546.9) * mm, v(216.44, 666.14) * mm, v(214.99, 762.12) * mm, v(212.08, 791.2) * mm, v(185.9, 802.83) * mm, v(162.64, 786.84) * mm, v(114.65, 475.65) * mm, v(121.92, 446.56) * mm, v(180.09, 346.23) * mm, v(201.9, 350.59) * mm, v(278.97, 437.84) * mm]});
            skFitSpline(sketch, "E34", {"points": [v(178.15, -355.19) * mm, v(211.05, -215.34) * mm, v(256.3, -48.77) * mm, v(298.84, 138.5) * mm, v(315.3, 306.1) * mm, v(308.1, 346.2) * mm, v(289.59, 348.26) * mm, v(227.9, 282.45) * mm, v(213.5, 254.69) * mm, v(142.55, -313.93) * mm], "startDerivative": vector(260.8, 1163.28) * mm, "endDerivative": vector(-357.18, -3242.65) * mm});
            skFitSpline(sketch, "E35", {"points": [v(178.15, -355.19) * mm, v(142.55, -313.93) * mm, v(88.15, -248.93) * mm, v(59.04, -211.08) * mm], "startDerivative": vector(-104.4, 120.4) * mm, "endDerivative": vector(-88.09, 117.81) * mm});
            skFitSpline(sketch, "E36", {"points": [v(88.15, -248.93) * mm, v(157.06, 256.72) * mm, v(156.1, 292.63) * mm, v(124.84, 337.91) * mm, v(112.58, 347.17) * mm, v(104.41, 330.29) * mm, v(84.68, 77.24) * mm, v(59.04, -211.08) * mm], "startDerivative": vector(302.64, 2248.83) * mm, "endDerivative": vector(-126.04, -1237.86) * mm});
            skLineSegment(sketch, "E37", {"start": v(170.59, -675.29) * mm, "end": v(170.59, -606.61) * mm});
            skLineSegment(sketch, "E38", {"start": v(156.62, -598.2) * mm, "end": v(130.78, -611.83) * mm});
            skLineSegment(sketch, "E39", {"start": v(125.7, -620.26) * mm, "end": v(125.7, -688.93) * mm});
            skLineSegment(sketch, "E40", {"start": v(139.68, -697.35) * mm, "end": v(165.51, -683.71) * mm});
            skLineSegment(sketch, "E41", {"start": v(91.74, -602.48) * mm, "end": v(91.74, -704.81) * mm});
            skLineSegment(sketch, "E42", {"start": v(86.66, -713.24) * mm, "end": v(57.67, -728.55) * mm});
            skLineSegment(sketch, "E43", {"start": v(43.7, -720.12) * mm, "end": v(43.7, -617.79) * mm});
            skLineSegment(sketch, "E44", {"start": v(48.77, -609.36) * mm, "end": v(77.77, -594.05) * mm});
            skPoint(sketch, "E45.visualSharp", {"position": v(170.59, -681.03) * mm});
            skArc(sketch, "E45.filletArc", {"start": v(165.51, -683.71) * mm, "mid": v(169.22, -680.2) * mm, "end": v(170.59, -675.29) * mm});
            skPoint(sketch, "E46.visualSharp", {"position": v(125.7, -614.51) * mm});
            skArc(sketch, "E46.filletArc", {"start": v(130.78, -611.83) * mm, "mid": v(127.07, -615.34) * mm, "end": v(125.7, -620.26) * mm});
            skPoint(sketch, "E47.visualSharp", {"position": v(125.7, -704.73) * mm});
            skArc(sketch, "E47.filletArc", {"start": v(125.7, -688.93) * mm, "mid": v(130.32, -697.09) * mm, "end": v(139.68, -697.35) * mm});
            skPoint(sketch, "E48.visualSharp", {"position": v(170.59, -590.81) * mm});
            skArc(sketch, "E48.filletArc", {"start": v(170.59, -606.61) * mm, "mid": v(165.98, -598.46) * mm, "end": v(156.62, -598.2) * mm});
            skPoint(sketch, "E49.visualSharp", {"position": v(43.7, -735.92) * mm});
            skArc(sketch, "E49.filletArc", {"start": v(43.7, -720.12) * mm, "mid": v(48.3, -728.28) * mm, "end": v(57.67, -728.55) * mm});
            skPoint(sketch, "E50.visualSharp", {"position": v(91.74, -586.68) * mm});
            skArc(sketch, "E50.filletArc", {"start": v(91.74, -602.48) * mm, "mid": v(87.13, -594.32) * mm, "end": v(77.77, -594.05) * mm});
            skPoint(sketch, "E51.visualSharp", {"position": v(91.74, -710.55) * mm});
            skArc(sketch, "E51.filletArc", {"start": v(86.66, -713.24) * mm, "mid": v(90.37, -709.73) * mm, "end": v(91.74, -704.81) * mm});
            skPoint(sketch, "E52.visualSharp", {"position": v(43.7, -612.05) * mm});
            skArc(sketch, "E52.filletArc", {"start": v(48.77, -609.36) * mm, "mid": v(45.06, -612.87) * mm, "end": v(43.7, -617.79) * mm});
            skSolve(sketch);
        }
        {
            var Q0;
            Q0=qSketchRegion(id+"F8",true);
            extrude(context, id + "F9", {"entities" : qUnion([Q0]), "operationType" : NewBodyOperationType.REMOVE, "endBound" : BoundingType.THROUGH_ALL, "oppositeDirection" : true, "depth" : 25.4 * mm, "hasSecondDirection" : true, "secondDirectionBound" : SecondDirectionBoundingType.THROUGH_ALL, "secondDirectionOppositeDirection" : false, "secondDirectionDepth" : 25.4 * mm});
        }
    });
